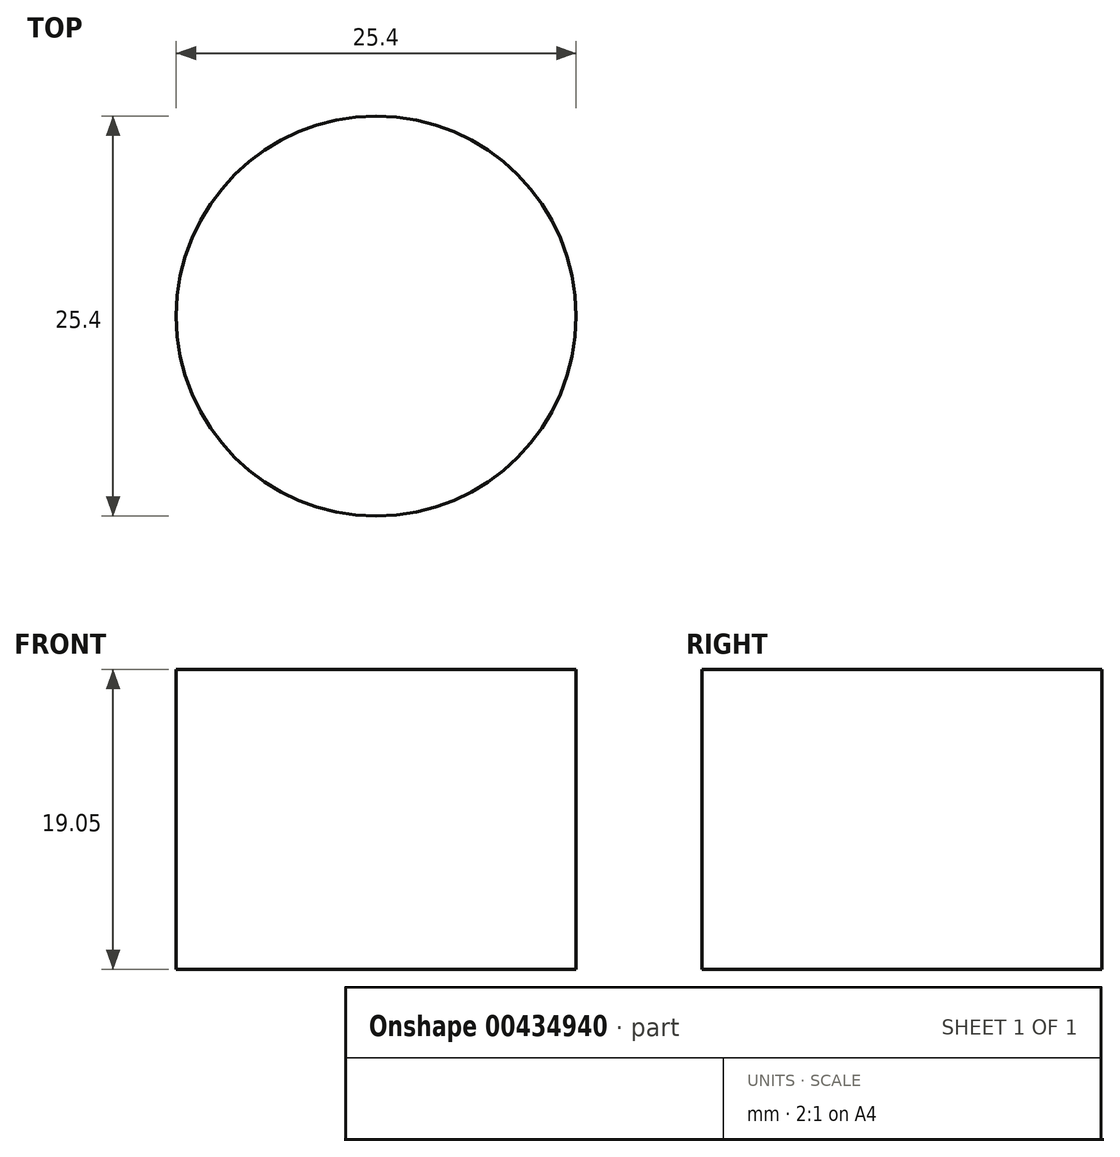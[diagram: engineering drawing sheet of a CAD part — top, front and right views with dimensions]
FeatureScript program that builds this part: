
annotation { "Feature Type Name" : "Feature", "Feature Type Description" : "" }
export const myFeature = defineFeature(function(context is Context, id is Id, definition is map)
    precondition{}
    {
        {
            var Q0;
            Q0=qCreatedBy(makeId("Top.planeOp"),FACE);
            var sketch = newSketch(context, id + "F0", { "sketchPlane" : qUnion([Q0])});
            skCircle(sketch, "E0", {"center": v(0, 0) * mm, "radius": 12.7 * mm});
            skSolve(sketch);
        }
        {
            var Q0;
            Q0 = qSketchRegion(id + "F0", true);
            extrude(context, id + "F1", {"entities" : qUnion([Q0]), "depth" : 19.05 * mm});
        }
    });
